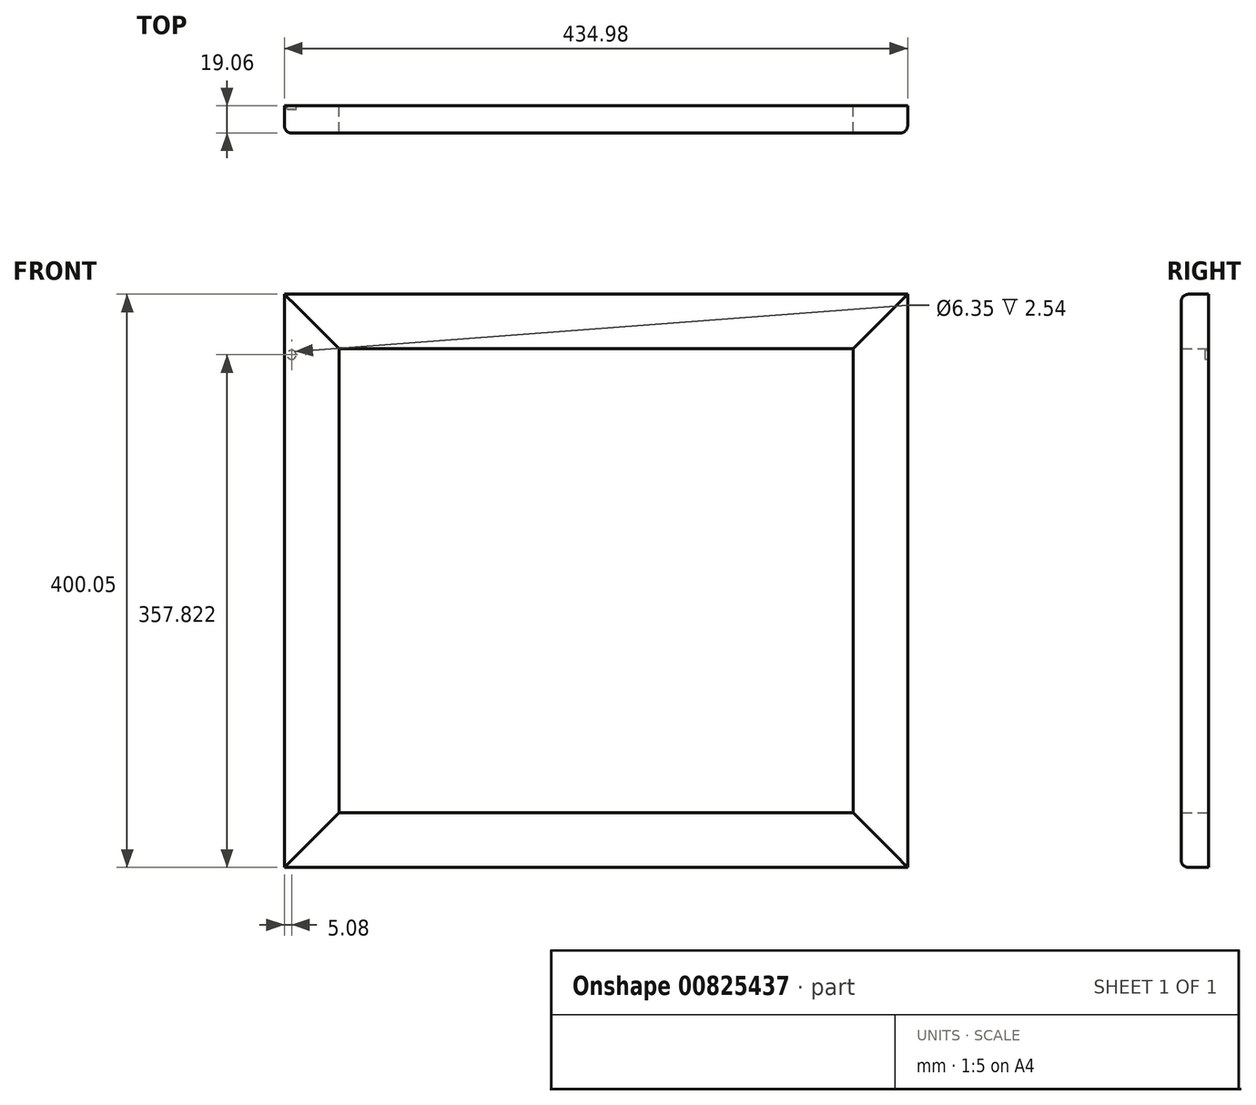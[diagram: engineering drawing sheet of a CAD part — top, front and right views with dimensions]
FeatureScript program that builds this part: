
annotation { "Feature Type Name" : "Feature", "Feature Type Description" : "" }
export const myFeature = defineFeature(function(context is Context, id is Id, definition is map)
    precondition{}
    {
        {
            assignVariable(context, id + "F0", {"name" : "thickness", "anyValue" : 19.05 * mm});
        }
        {
            var Q0;
            Q0=qCreatedBy(makeId("Front.planeOp"),FACE);
            var sketch = newSketch(context, id + "F1", { "sketchPlane" : qUnion([Q0])});
            skLineSegment(sketch, "E0.left", {"start": v(0, 0) * mm, "end": v(0, 400.05) * mm});
            skLineSegment(sketch, "E0.right", {"start": v(38.1, 38.1) * mm, "end": v(38.1, 361.95) * mm});
            skLineSegment(sketch, "E1", {"start": v(0, 400.05) * mm, "end": v(38.1, 361.95) * mm});
            skLineSegment(sketch, "E2", {"start": v(0, 0) * mm, "end": v(38.1, 38.1) * mm});
            skSolve(sketch);
        }
        {
            var Q0;
            Q0=qSketchRegion(id+"F1",true);
            extrude(context, id + "F2", {"entities" : qUnion([Q0]), "endBound" : BoundingType.SYMMETRIC, "depth" : getVariable(context, 'thickness'), "offsetDistance" : 25.4 * mm});
        }
        {
            var Q0;
            Q0=qCreatedBy(makeId("Front.planeOp"),FACE);
            var sketch = newSketch(context, id + "F3", { "sketchPlane" : qUnion([Q0])});
            skLineSegment(sketch, "E3.bottom", {"start": v(0, 0) * mm, "end": v(434.98, 0) * mm});
            skLineSegment(sketch, "E3.top", {"start": v(38.1, 38.1) * mm, "end": v(396.88, 38.1) * mm});
            skLineSegment(sketch, "E4", {"start": v(0, 0) * mm, "end": v(38.1, 38.1) * mm});
            skLineSegment(sketch, "E5", {"start": v(434.98, 0) * mm, "end": v(396.88, 38.1) * mm});
            skSolve(sketch);
        }
        {
            var Q0;
            Q0=qSketchRegion(id+"F3",true);
            extrude(context, id + "F4", {"entities" : qUnion([Q0]), "endBound" : BoundingType.SYMMETRIC, "depth" : 19.05 * mm, "offsetDistance" : 25.4 * mm});
        }
        {
            var Q0;
            Q0=makeQuery(id+"F4.opExtrude","CAP_EDGE",EDGE,{"disambiguationData":[OSD([sQuery(id+"F3.wireOp",EDGE,"E3.top")])],"isStart":false});
            cPoint(context, id + "F5", {"entities" : qUnion([Q0]), "parameter" : 0.5});
        }
        {
            var Q0;
            Q0=qCreatedBy(makeId("Right.planeOp"),FACE);
            var Q1;
            Q1=qCreatedBy(id+"F5",VERTEX);
            cPlane(context, id + "F6", {"entities" : qUnion([Q0, Q1]), "cplaneType" : CPlaneType.PLANE_POINT, "offset" : 25.4 * mm, "width" : 152.4 * mm, "height" : 152.4 * mm});
        }
        {
            var Q0;
            Q0=makeQuery(id+"F2.opExtrude","SWEPT_BODY",BODY,{"disambiguationData":[OSD([sQuery(id+"F1.wireOp",EDGE,"E0.left"),sQuery(id+"F1.wireOp",EDGE,"E0.right"),sQuery(id+"F1.wireOp",EDGE,"E1"),sQuery(id+"F1.wireOp",EDGE,"E2")])]});
            var Q1;
            Q1=qCreatedBy(id+"F6.planeOp",FACE);
            mirror(context, id + "F7", {"entities" : qUnion([Q0]), "mirrorPlane" : qUnion([Q1])});
        }
        {
            var Q0;
            Q0=makeQuery(id+"F2.opExtrude","CAP_EDGE",EDGE,{"disambiguationData":[OSD([sQuery(id+"F1.wireOp",EDGE,"E0.left")])],"isStart":false});
            cPoint(context, id + "F8", {"entities" : qUnion([Q0]), "parameter" : 0.5});
        }
        {
            var Q0;
            Q0=qCreatedBy(makeId("Top.planeOp"),FACE);
            var Q1;
            Q1=qCreatedBy(id+"F8",VERTEX);
            cPlane(context, id + "F9", {"entities" : qUnion([Q0, Q1]), "cplaneType" : CPlaneType.PLANE_POINT, "offset" : 25.4 * mm, "width" : 152.4 * mm, "height" : 152.4 * mm});
        }
        {
            var Q0;
            Q0=makeQuery(id+"F4.opExtrude","SWEPT_BODY",BODY,{"disambiguationData":[OSD([sQuery(id+"F3.wireOp",EDGE,"E3.bottom"),sQuery(id+"F3.wireOp",EDGE,"E3.top"),sQuery(id+"F3.wireOp",EDGE,"E4"),sQuery(id+"F3.wireOp",EDGE,"E5")])]});
            var Q1;
            Q1=qCreatedBy(id+"F9.planeOp",FACE);
            mirror(context, id + "F10", {"entities" : qUnion([Q0]), "mirrorPlane" : qUnion([Q1])});
        }
        {
            var Q0;
            Q0=makeQuery(id+"F2.opExtrude","CAP_FACE",FACE,{"disambiguationData":[OSD([sQuery(id+"F1.wireOp",EDGE,"E0.left"),sQuery(id+"F1.wireOp",EDGE,"E0.right"),sQuery(id+"F1.wireOp",EDGE,"E1"),sQuery(id+"F1.wireOp",EDGE,"E2")])],"isStart":true});
            var sketch = newSketch(context, id + "F11", { "sketchPlane" : qUnion([Q0])});
            skCircle(sketch, "E6", {"center": v(-5.08, 357.82) * mm, "radius": 3.18 * mm});
            skSolve(sketch);
        }
        {
            var Q0;
            Q0=qSketchRegion(id+"F11",true);
            extrude(context, id + "F12", {"entities" : qUnion([Q0]), "operationType" : NewBodyOperationType.REMOVE, "oppositeDirection" : true, "depth" : 2.54 * mm, "offsetDistance" : 25.4 * mm});
        }
        {
            var Q0;
            Q0=makeQuery(id+"F2.opExtrude","CAP_EDGE",EDGE,{"disambiguationData":[OSD([sQuery(id+"F1.wireOp",EDGE,"E0.left")])],"isStart":false});
            var Q1;
            Q1=makeQuery(id+"F4.opExtrude","CAP_EDGE",EDGE,{"disambiguationData":[OSD([sQuery(id+"F3.wireOp",EDGE,"E3.bottom")])],"isStart":false});
            var Q2;
            Q2=makeQuery(id+"F7.opPattern","COPY",EDGE,{"derivedFrom":makeQuery(id+"F2.opExtrude","CAP_EDGE",EDGE,{"disambiguationData":[OSD([sQuery(id+"F1.wireOp",EDGE,"E0.left")])],"isStart":false}),"instanceName":"1"});
            var Q3;
            Q3=makeQuery(id+"F10.opPattern","COPY",EDGE,{"derivedFrom":makeQuery(id+"F4.opExtrude","CAP_EDGE",EDGE,{"disambiguationData":[OSD([sQuery(id+"F3.wireOp",EDGE,"E3.bottom")])],"isStart":false}),"instanceName":"1"});
            fillet(context, id + "F13", {"entities" : qUnion([Q0, Q1, Q2, Q3]), "radius" : 5.08 * mm, "tangentPropagation" : true, "allowEdgeOverflow" : false});
        }
    });
